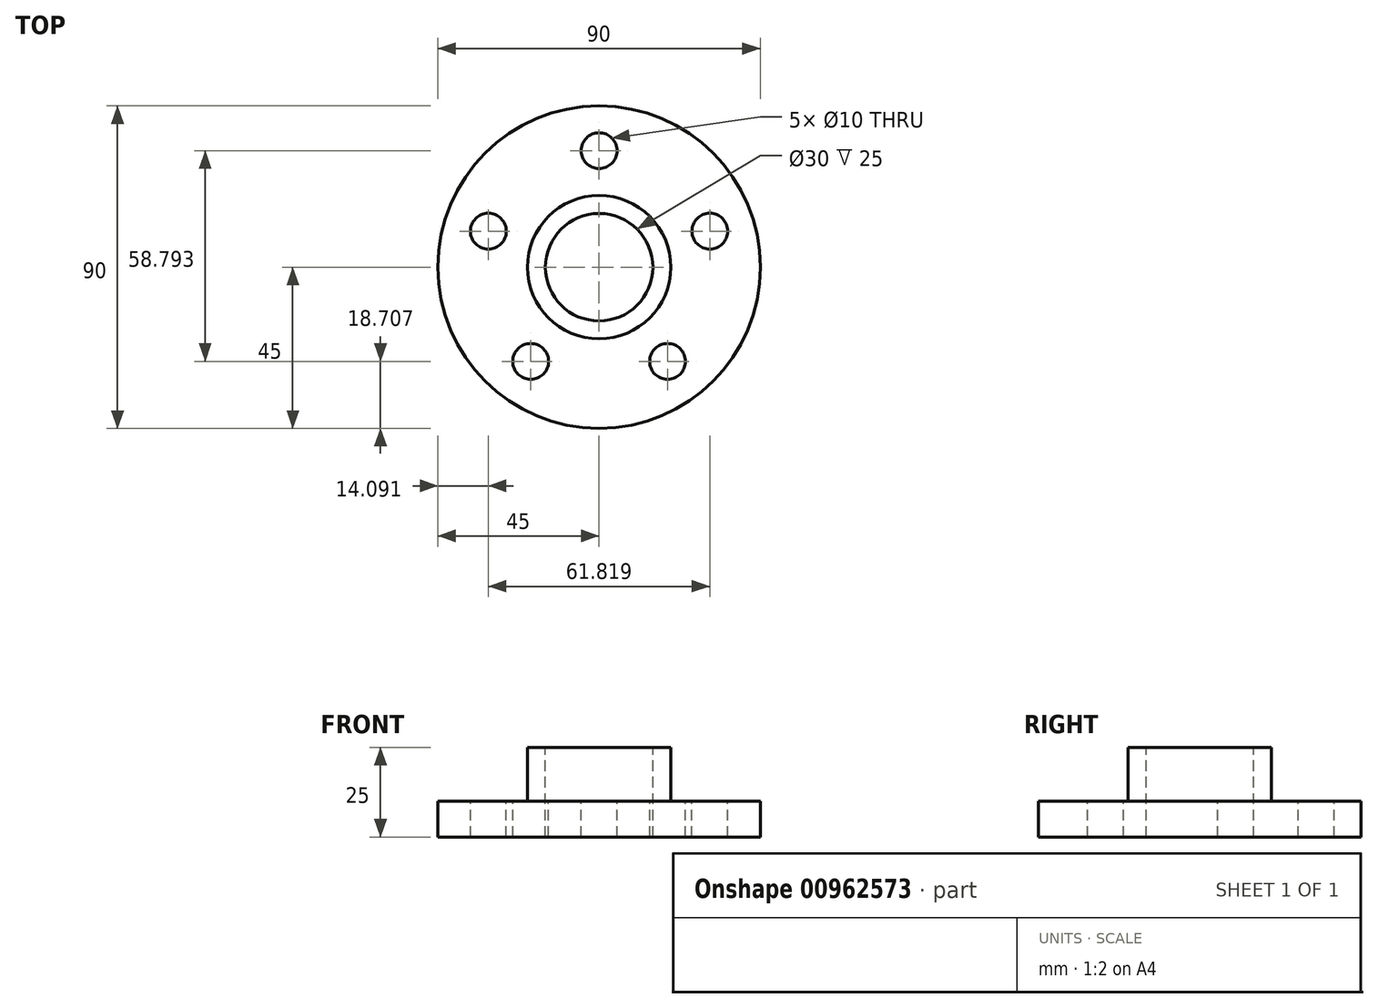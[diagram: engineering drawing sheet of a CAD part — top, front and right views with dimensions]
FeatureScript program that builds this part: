
annotation { "Feature Type Name" : "Feature", "Feature Type Description" : "" }
export const myFeature = defineFeature(function(context is Context, id is Id, definition is map)
    precondition{}
    {
        {
            var Q0;
            Q0=qCreatedBy(makeId("Front.planeOp"),FACE);
            var sketch = newSketch(context, id + "F0", { "sketchPlane" : qUnion([Q0])});
            skLineSegment(sketch, "E0", {"start": v(0, 35.7) * mm, "end": v(0, 0) * mm});
            skLineSegment(sketch, "E1", {"start": v(15, 25) * mm, "end": v(15, 0) * mm});
            skLineSegment(sketch, "E2", {"start": v(15, 0) * mm, "end": v(45, 0) * mm});
            skLineSegment(sketch, "E3", {"start": v(45, 0) * mm, "end": v(45, 10) * mm});
            skLineSegment(sketch, "E4", {"start": v(45, 10) * mm, "end": v(20, 10) * mm});
            skLineSegment(sketch, "E5", {"start": v(20, 10) * mm, "end": v(20, 25) * mm});
            skLineSegment(sketch, "E6", {"start": v(20, 25) * mm, "end": v(15, 25) * mm});
            skSolve(sketch);
        }
        {
            var Q0;
            Q0 = qSketchRegion(id + "F0", true);
            var Q1;
            Q1=sQuery(id+"F0.wireOp",EDGE,"E0");
            revolve(context, id + "F1", {"surfaceOperationType" : NewSurfaceOperationType.NEW, "entities" : qUnion([Q0]), "axis" : qUnion([Q1]), "revolveType" : RevolveType.FULL});
        }
        {
            var Q0;
            Q0=makeQuery(id+"F1.opRevolve","SWEPT_FACE",FACE,{"disambiguationData":[OSD([sQuery(id+"F0.wireOp",EDGE,"E4")])]});
            var sketch = newSketch(context, id + "F2", { "sketchPlane" : qUnion([Q0])});
            skCircle(sketch, "E7", {"center": v(0, 0) * mm, "radius": 32.5 * mm});
            skCircle(sketch, "E8", {"center": v(0, 32.5) * mm, "radius": 5 * mm});
            skCircle(sketch, "E9.1.0", {"center": v(-30.9, 10.04) * mm, "radius": 5 * mm});
            skCircle(sketch, "E9.2.0", {"center": v(-19.1, -26.3) * mm, "radius": 5 * mm});
            skCircle(sketch, "E9.3.0", {"center": v(19.1, -26.3) * mm, "radius": 5 * mm});
            skCircle(sketch, "E9.4.0", {"center": v(30.9, 10.04) * mm, "radius": 5 * mm});
            skSolve(sketch);
        }
        {
            var Q0;
            {var subQ0=sQuery(id+"F2.wireOp",EDGE,"E9.3.0");var subQ1=sQuery(id+"F2.wireOp",EDGE,"E7");var subQ2=makeQuery(id+"F2.imprint","INTERSECT",VERTEX,{"disambiguationData":[OD(0.0)],"derivedFrom":[subQ1,subQ0]});Q0=makeQuery(id+"F2.imprint","IMPRINT",FACE,{"disambiguationData":[TD([[makeQuery(id+"F2.imprint","IMPRINT",EDGE,{"disambiguationData":[TD([[subQ2,-1.0]])],"derivedFrom":subQ1}),-1.0]])]});}
            var Q1;
            {var subQ0=sQuery(id+"F2.wireOp",EDGE,"E9.3.0");var subQ1=sQuery(id+"F2.wireOp",EDGE,"E7");var subQ2=makeQuery(id+"F2.imprint","INTERSECT",VERTEX,{"disambiguationData":[OD(0.0)],"derivedFrom":[subQ1,subQ0]});Q1=makeQuery(id+"F2.imprint","IMPRINT",FACE,{"disambiguationData":[TD([[makeQuery(id+"F2.imprint","IMPRINT",EDGE,{"disambiguationData":[TD([[subQ2,-1.0]])],"derivedFrom":subQ1}),1.0]])]});}
            var Q2;
            {var subQ0=sQuery(id+"F2.wireOp",EDGE,"E9.4.0");var subQ1=sQuery(id+"F2.wireOp",EDGE,"E7");var subQ2=makeQuery(id+"F2.imprint","INTERSECT",VERTEX,{"disambiguationData":[OD(0.0)],"derivedFrom":[subQ1,subQ0]});Q2=makeQuery(id+"F2.imprint","IMPRINT",FACE,{"disambiguationData":[TD([[makeQuery(id+"F2.imprint","IMPRINT",EDGE,{"disambiguationData":[TD([[subQ2,1.0]])],"derivedFrom":subQ1}),1.0]])]});}
            var Q3;
            {var subQ0=sQuery(id+"F2.wireOp",EDGE,"E9.4.0");var subQ1=sQuery(id+"F2.wireOp",EDGE,"E7");var subQ2=makeQuery(id+"F2.imprint","INTERSECT",VERTEX,{"disambiguationData":[OD(0.0)],"derivedFrom":[subQ1,subQ0]});Q3=makeQuery(id+"F2.imprint","IMPRINT",FACE,{"disambiguationData":[TD([[makeQuery(id+"F2.imprint","IMPRINT",EDGE,{"disambiguationData":[TD([[subQ2,1.0]])],"derivedFrom":subQ1}),-1.0]])]});}
            var Q4;
            {var subQ0=sQuery(id+"F2.wireOp",EDGE,"E8");var subQ1=sQuery(id+"F2.wireOp",EDGE,"E7");var subQ2=makeQuery(id+"F2.imprint","INTERSECT",VERTEX,{"disambiguationData":[OD(0.0)],"derivedFrom":[subQ1,subQ0]});Q4=makeQuery(id+"F2.imprint","IMPRINT",FACE,{"disambiguationData":[TD([[makeQuery(id+"F2.imprint","IMPRINT",EDGE,{"disambiguationData":[TD([[subQ2,-1.0]])],"derivedFrom":subQ1}),-1.0]])]});}
            var Q5;
            {var subQ0=sQuery(id+"F2.wireOp",EDGE,"E8");var subQ1=sQuery(id+"F2.wireOp",EDGE,"E7");var subQ2=makeQuery(id+"F2.imprint","INTERSECT",VERTEX,{"disambiguationData":[OD(0.0)],"derivedFrom":[subQ1,subQ0]});Q5=makeQuery(id+"F2.imprint","IMPRINT",FACE,{"disambiguationData":[TD([[makeQuery(id+"F2.imprint","IMPRINT",EDGE,{"disambiguationData":[TD([[subQ2,-1.0]])],"derivedFrom":subQ1}),1.0]])]});}
            var Q6;
            {var subQ0=sQuery(id+"F2.wireOp",EDGE,"E9.1.0");var subQ1=sQuery(id+"F2.wireOp",EDGE,"E7");var subQ2=makeQuery(id+"F2.imprint","INTERSECT",VERTEX,{"disambiguationData":[OD(0.0)],"derivedFrom":[subQ1,subQ0]});Q6=makeQuery(id+"F2.imprint","IMPRINT",FACE,{"disambiguationData":[TD([[makeQuery(id+"F2.imprint","IMPRINT",EDGE,{"disambiguationData":[TD([[subQ2,-1.0]])],"derivedFrom":subQ1}),-1.0]])]});}
            var Q7;
            {var subQ0=sQuery(id+"F2.wireOp",EDGE,"E9.1.0");var subQ1=sQuery(id+"F2.wireOp",EDGE,"E7");var subQ2=makeQuery(id+"F2.imprint","INTERSECT",VERTEX,{"disambiguationData":[OD(0.0)],"derivedFrom":[subQ1,subQ0]});Q7=makeQuery(id+"F2.imprint","IMPRINT",FACE,{"disambiguationData":[TD([[makeQuery(id+"F2.imprint","IMPRINT",EDGE,{"disambiguationData":[TD([[subQ2,-1.0]])],"derivedFrom":subQ1}),1.0]])]});}
            var Q8;
            {var subQ0=sQuery(id+"F2.wireOp",EDGE,"E9.2.0");var subQ1=sQuery(id+"F2.wireOp",EDGE,"E7");var subQ2=makeQuery(id+"F2.imprint","INTERSECT",VERTEX,{"disambiguationData":[OD(0.0)],"derivedFrom":[subQ1,subQ0]});Q8=makeQuery(id+"F2.imprint","IMPRINT",FACE,{"disambiguationData":[TD([[makeQuery(id+"F2.imprint","IMPRINT",EDGE,{"disambiguationData":[TD([[subQ2,-1.0]])],"derivedFrom":subQ1}),-1.0]])]});}
            var Q9;
            {var subQ0=sQuery(id+"F2.wireOp",EDGE,"E9.2.0");var subQ1=sQuery(id+"F2.wireOp",EDGE,"E7");var subQ2=makeQuery(id+"F2.imprint","INTERSECT",VERTEX,{"disambiguationData":[OD(0.0)],"derivedFrom":[subQ1,subQ0]});Q9=makeQuery(id+"F2.imprint","IMPRINT",FACE,{"disambiguationData":[TD([[makeQuery(id+"F2.imprint","IMPRINT",EDGE,{"disambiguationData":[TD([[subQ2,-1.0]])],"derivedFrom":subQ1}),1.0]])]});}
            extrude(context, id + "F3", {"entities" : qUnion([Q0, Q1, Q2, Q3, Q4, Q5, Q6, Q7, Q8, Q9]), "operationType" : NewBodyOperationType.REMOVE, "endBound" : BoundingType.THROUGH_ALL, "oppositeDirection" : true, "depth" : 25 * mm, "offsetDistance" : 25 * mm});
        }
    });
